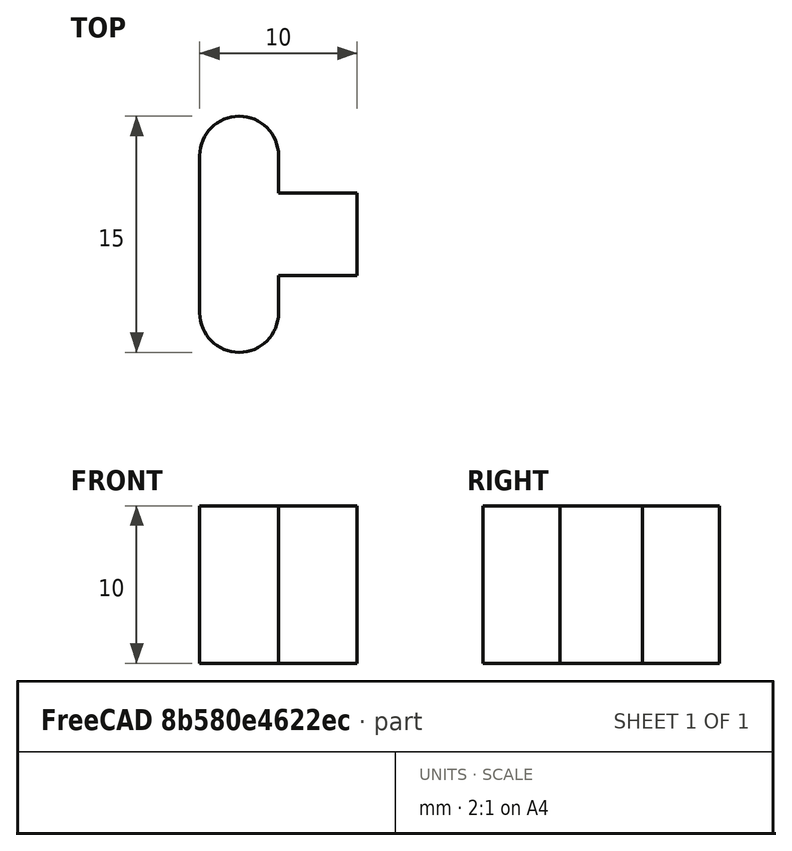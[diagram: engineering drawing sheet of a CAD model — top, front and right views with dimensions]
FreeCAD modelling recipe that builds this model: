
FCSTD DOCUMENT  (FreeCAD 0.17R13541 (Git))
Label: C-skenaBendTool
License: All rights reserved
LicenseURL: http://en.wikipedia.org/wiki/All_rights_reserved
objects: Sketcher::SketchObject×1, PartDesign::Pad×1, PartDesign::Body×1
note: 4 computed .brp shape members not serialized (recipe doc carries the construction recipe); baked Part::Feature solids carry a one-line shape summary decoded from their .brp

FEATURE [Sketcher::SketchObject] Sketch
  MapMode = 5
  Support = -> [XY_Plane]
  expr: Constraints.innerHeight = 15mm - 2 * Constraints.baserad
  sketch-geometry (8):
    g0: ArcOfCircle CenterX=0 CenterY=0 CenterZ=0 NormalX=0 NormalY=0 NormalZ=1 AngleXU=0 Radius=2.5 StartAngle=0 EndAngle=3.14159
    g1: LineSegment StartX=-2.5 StartY=0 StartZ=0 EndX=-2.5 EndY=-10 EndZ=0
    g2: ArcOfCircle CenterX=0 CenterY=-10 CenterZ=0 NormalX=0 NormalY=0 NormalZ=1 AngleXU=0 Radius=2.5 StartAngle=3.14159 EndAngle=6.28319
    g3: LineSegment StartX=2.5 StartY=0 StartZ=0 EndX=2.5 EndY=-2.375 EndZ=0
    g4: LineSegment StartX=2.5 StartY=-2.375 StartZ=0 EndX=7.5 EndY=-2.375 EndZ=0
    g5: LineSegment StartX=7.5 StartY=-2.375 StartZ=0 EndX=7.5 EndY=-7.625 EndZ=0
    g6: LineSegment StartX=7.5 StartY=-7.625 StartZ=0 EndX=2.5 EndY=-7.625 EndZ=0
    g7: LineSegment StartX=2.5 StartY=-7.625 StartZ=0 EndX=2.5 EndY=-10 EndZ=0
  constraints (26):
    c: Coincident(g0,g-1)
    c: PointOnObject(g0,g-1)
    c: PointOnObject(g0,g-1)
    c: Coincident(g1,g0)
    c: Vertical(g1)
    c: PointOnObject(g2,g-2)
    c: Coincident(g2,g1)
    c: Coincident(g3,g0)
    c: Vertical(g3)
    c: Coincident(g4,g3)
    c: Horizontal(g4)
    c: Vertical(g5)
    c: Coincident(g6,g5)
    c: Horizontal(g6)
    c: Coincident(g7,g6)
    c: Coincident(g7,g2)
    c: Radius(g0) = 2.5  'baserad'
    c: DistanceY(g1,g1) = 10  'innerHeight'
    c: Coincident(g4,g5)
    c: DistanceY(g5,g5) = 5.25  'opening'
    c: Equal(g3,g7)
    c: Equal(g0,g4)
    c: Equal(g4,g6)
    c: DistanceX(g0,g4) = 10
    c: Horizontal(g1,g2)
    c: Horizontal(g2,g2)
FEATURE [PartDesign::Pad] Pad
  Length = 10
  Length2 = 100
  Profile = -> Sketch
  Type = 0
FEATURE [PartDesign::Body] Body
  Group = -> [Sketch,Pad]
  Origin = -> Origin
  Tip = -> Pad
